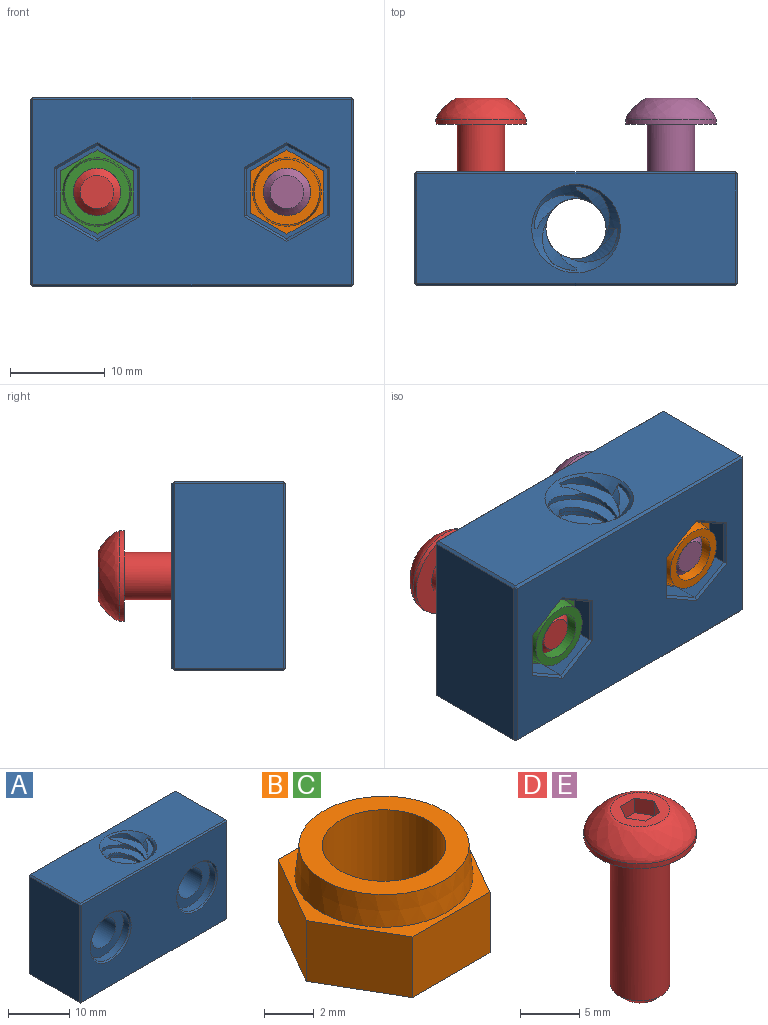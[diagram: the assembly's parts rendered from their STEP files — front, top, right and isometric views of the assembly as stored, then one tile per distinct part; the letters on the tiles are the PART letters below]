
ASSEMBLY  parts=5 mates=2
PART A: 88 faces, bbox 34x12x21.5 mm
  f0: bspline ~20.25x8.84mm, area 73.1mm2, adj f1,f18,f20,f85,f86
  f1: cylinder r=4.42mm len=19.5mm, axis (0,0,-1), area 67.9mm2, adj f0,f2,f12,f20,f84,f86
  f2: bspline ~20.25x8.84mm, area 73.1mm2, adj f1,f12,f19,f84,f86
  f3: bspline ~20.25x8.84mm, area 73.1mm2, adj f4,f17,f21,f84,f86,f87
  f4: cylinder r=4.42mm len=19.5mm, axis (0,0,-1), area 67.9mm2, adj f3,f5,f13,f21,f84,f86
  f5: bspline ~20.25x8.84mm, area 73.1mm2, adj f4,f13,f18,f84,f85,f86
  f6: bspline ~20.25x8.84mm, area 73.1mm2, adj f7,f16,f22,f84,f86
  f7: cylinder r=4.42mm len=19.5mm, axis (0,0,-1), area 67.9mm2, adj f6,f8,f14,f22,f84,f86
  f8: bspline ~20.25x8.84mm, area 73.1mm2, adj f7,f14,f17,f84,f87
  f9: bspline ~20.25x8.84mm, area 73.1mm2, adj f10,f19,f23,f84,f86
  f10: cylinder r=4.42mm len=19.5mm, axis (0,0,-1), area 67.9mm2, adj f9,f11,f15,f23,f84,f86
  f11: bspline ~20.25x8.84mm, area 73.1mm2, adj f10,f15,f16,f84,f86
  f12: plane 0.31x0.31mm, normal (0,-1,0), area 0mm2, adj f1,f2,f86
  f13: plane 0.31x0.31mm, normal (1,0,0), area 0mm2, adj f4,f5,f86
  f14: plane 0.31x0.31mm, normal (0,1,0), area 0mm2, adj f7,f8,f86
  f15: plane 0.31x0.31mm, normal (-1,0,0), area 0mm2, adj f10,f11,f86
  f16: cylinder r=3.17mm len=17mm, axis (0,0,-1), area 21.1mm2, adj f6,f11,f84,f86
  f17: cylinder r=3.17mm len=17mm, axis (0,0,-1), area 21.1mm2, adj f3,f8,f84,f87
  f18: cylinder r=3.17mm len=17mm, axis (0,0,-1), area 21.1mm2, adj f0,f5,f85,f86
  f19: cylinder r=3.17mm len=17mm, axis (0,0,-1), area 21.1mm2, adj f2,f9,f84,f86
  f20: plane 0.31x0.31mm, normal (0,-1,0), area 0mm2, adj f0,f1,f84
  f21: plane 0.31x0.31mm, normal (1,0,0), area 0mm2, adj f3,f4,f84
  f22: plane 0.31x0.31mm, normal (0,1,0), area 0mm2, adj f6,f7,f84
  f23: plane 0.31x0.31mm, normal (-1,0,0), area 0mm2, adj f9,f10,f84
  f24: plane 33.5x11.5mm, normal (0,0,1), area 316.8mm2, adj f58,f63,f66,f69,f84
  f25: cylinder r=2.75mm len=5.5mm, axis (0,-1,0), area 93.3mm2, adj f34,f36
  f26: cylinder r=2.75mm len=5.5mm, axis (0,-1,0), area 93.3mm2, adj f32,f43
  f27: plane 33.5x19.5mm, normal (0,1,0), area 513mm2, adj f53,f54,f63,f64,f72,f73,f74,f75
  f28: plane 33.5x19.5mm, normal (0,-1,0), area 511.5mm2, adj f56,f57,f65,f66,f70,f71
  f29: plane 19.5x11.5mm, normal (1,0,0), area 224.2mm2, adj f55,f64,f65,f69
  f30: plane 19.5x11.5mm, normal (-1,0,0), area 224.2mm2, adj f50,f53,f57,f58
  f31: plane 33.5x11.5mm, normal (0,0,-1), area 316.8mm2, adj f50,f54,f55,f56,f86
  f32: plane 9x9mm, normal (0,-1,0), area 39.9mm2, adj f26,f33
  f33: cylinder r=4.5mm len=9mm, axis (0,-1,0), area 38.2mm2, adj f32,f70
  f34: plane 9x9mm, normal (0,-1,0), area 39.9mm2, adj f25,f35
  f35: cylinder r=4.5mm len=9mm, axis (0,-1,0), area 38.2mm2, adj f34,f71
  f36: plane 9.82x8.5mm, normal (0,1,0), area 38.8mm2, adj f25,f37,f38,f39,f40,f41,f42
  f37: plane 4.91x4.75mm, normal (-1,0,0), area 23.3mm2, adj f36,f38,f42,f83
  f38: plane 4.75x4.25mm, normal (-0.5,0,0.87), area 23.3mm2, adj f36,f37,f39,f81
  f39: plane 4.75x4.25mm, normal (0.5,0,0.87), area 23.3mm2, adj f36,f38,f40,f79
  f40: plane 4.91x4.75mm, normal (1,0,0), area 23.3mm2, adj f36,f39,f41,f78
  f41: plane 4.75x4.25mm, normal (0.5,0,-0.87), area 23.3mm2, adj f36,f40,f42,f80
  f42: plane 4.75x4.25mm, normal (-0.5,0,-0.87), area 23.3mm2, adj f36,f37,f41,f82
  f43: plane 9.82x8.5mm, normal (0,1,0), area 38.8mm2, adj f26,f44,f45,f46,f47,f48,f49
  f44: plane 4.75x4.25mm, normal (0.5,0,-0.87), area 23.3mm2, adj f43,f45,f49,f75
  f45: plane 4.75x4.25mm, normal (-0.5,0,-0.87), area 23.3mm2, adj f43,f44,f46,f77
  f46: plane 4.91x4.75mm, normal (-1,0,0), area 23.3mm2, adj f43,f45,f47,f76
  f47: plane 4.75x4.25mm, normal (-0.5,0,0.87), area 23.3mm2, adj f43,f46,f48,f74
  f48: plane 4.75x4.25mm, normal (0.5,0,0.87), area 23.3mm2, adj f43,f47,f49,f72
  f49: plane 4.91x4.75mm, normal (1,0,0), area 23.3mm2, adj f43,f44,f48,f73
  f50: plane 11.5x0.25mm, normal (-0.71,0,-0.71), area 4.1mm2, adj f30,f31,f51,f52
  f51: plane 0.25x0.25mm, normal (-0.58,0.58,-0.58), area 0.1mm2, adj f50,f53,f54
  f52: plane 0.25x0.25mm, normal (-0.58,-0.58,-0.58), area 0.1mm2, adj f50,f56,f57
  f53: plane 19.5x0.25mm, normal (-0.71,0.71,0), area 6.9mm2, adj f27,f30,f51,f59
  f54: plane 33.5x0.25mm, normal (0,0.71,-0.71), area 11.8mm2, adj f27,f31,f51,f60
  f55: plane 11.5x0.25mm, normal (0.71,0,-0.71), area 4.1mm2, adj f29,f31,f60,f61
  f56: plane 33.5x0.25mm, normal (0,-0.71,-0.71), area 11.8mm2, adj f28,f31,f52,f61
  f57: plane 19.5x0.25mm, normal (-0.71,-0.71,0), area 6.9mm2, adj f28,f30,f52,f62
  f58: plane 11.5x0.25mm, normal (-0.71,0,0.71), area 4.1mm2, adj f24,f30,f59,f62
  f59: plane 0.25x0.25mm, normal (-0.58,0.58,0.58), area 0.1mm2, adj f53,f58,f63
  f60: plane 0.25x0.25mm, normal (0.58,0.58,-0.58), area 0.1mm2, adj f54,f55,f64
  f61: plane 0.25x0.25mm, normal (0.58,-0.58,-0.58), area 0.1mm2, adj f55,f56,f65
  f62: plane 0.25x0.25mm, normal (-0.58,-0.58,0.58), area 0.1mm2, adj f57,f58,f66
  f63: plane 33.5x0.25mm, normal (0,0.71,0.71), area 11.8mm2, adj f24,f27,f59,f67
  f64: plane 19.5x0.25mm, normal (0.71,0.71,0), area 6.9mm2, adj f27,f29,f60,f67
  f65: plane 19.5x0.25mm, normal (0.71,-0.71,0), area 6.9mm2, adj f28,f29,f61,f68
  f66: plane 33.5x0.25mm, normal (0,-0.71,0.71), area 11.8mm2, adj f24,f28,f62,f68
  f67: plane 0.25x0.25mm, normal (0.58,0.58,0.58), area 0.1mm2, adj f63,f64,f69
  f68: plane 0.25x0.25mm, normal (0.58,-0.58,0.58), area 0.1mm2, adj f65,f66,f69
  f69: plane 11.5x0.25mm, normal (0.71,0,0.71), area 4.1mm2, adj f24,f29,f67,f68
  f70: cone r=4.5mm half-angle=45deg, axis (0,-1,0), area 10.3mm2, adj f28,f33
  f71: cone r=4.5mm half-angle=45deg, axis (0,-1,0), area 10.3mm2, adj f28,f35
  f72: plane 4.5x2.74mm, normal (0.35,0.71,0.61), area 1.8mm2, adj f27,f48,f73,f74
  f73: plane 5.2x0.25mm, normal (0.71,0.71,0), area 1.8mm2, adj f27,f49,f72,f75
  f74: plane 4.5x2.74mm, normal (-0.35,0.71,0.61), area 1.8mm2, adj f27,f47,f72,f76
  f75: plane 4.5x2.74mm, normal (0.35,0.71,-0.61), area 1.8mm2, adj f27,f44,f73,f77
  f76: plane 5.2x0.25mm, normal (-0.71,0.71,0), area 1.8mm2, adj f27,f46,f74,f77
  f77: plane 4.5x2.74mm, normal (-0.35,0.71,-0.61), area 1.8mm2, adj f27,f45,f75,f76
  f78: plane 5.2x0.25mm, normal (0.71,0.71,0), area 1.8mm2, adj f27,f40,f79,f80
  f79: plane 4.5x2.74mm, normal (0.35,0.71,0.61), area 1.8mm2, adj f27,f39,f78,f81
  f80: plane 4.5x2.74mm, normal (0.35,0.71,-0.61), area 1.8mm2, adj f27,f41,f78,f82
  f81: plane 4.5x2.74mm, normal (-0.35,0.71,0.61), area 1.8mm2, adj f27,f38,f79,f83
  f82: plane 4.5x2.74mm, normal (-0.35,0.71,-0.61), area 1.8mm2, adj f27,f42,f80,f83
  f83: plane 5.2x0.25mm, normal (-0.71,0.71,0), area 1.8mm2, adj f27,f37,f81,f82
  f84: cone r=3.17mm half-angle=45deg, axis (0,0,1), area 25.6mm2, adj f1,f2,f3,f4,f5,f6,f7,f8
  f85: cone r=3.17mm half-angle=45deg, axis (0,0,1), area 1.3mm2, adj f0,f5,f18,f84
  f86: cone r=3.17mm half-angle=45deg, axis (0,0,-1), area 25.6mm2, adj f0,f1,f2,f3,f4,f5,f6,f7
  f87: cone r=3.17mm half-angle=45deg, axis (0,0,-1), area 1.3mm2, adj f3,f8,f17,f86
PART B: 11 faces, bbox 8.9x7.7x4.5 mm
  f0: plane 3.84x3mm, normal (-0.87,0.5,0), area 13.3mm2, adj f1,f5,f6,f7
  f1: plane 3.84x3mm, normal (-0.87,-0.5,0), area 13.3mm2, adj f0,f2,f6,f7
  f2: plane 4.43x3mm, normal (0,-1,0), area 13.3mm2, adj f1,f3,f6,f7
  f3: plane 3.84x3mm, normal (0.87,-0.5,0), area 13.3mm2, adj f2,f4,f6,f7
  f4: plane 3.84x3mm, normal (0.87,0.5,0), area 13.3mm2, adj f3,f5,f6,f7
  f5: plane 4.43x3mm, normal (0,1,0), area 13.3mm2, adj f0,f4,f6,f7
  f6: plane 8.87x7.68mm, normal (0,0,1), area 10.4mm2, adj f0,f1,f2,f3,f4,f5,f8
  f7: plane 8.87x7.68mm, normal (0,0,-1), area 31.4mm2, adj f0,f1,f2,f3,f4,f5,f10
  f8: cone r=3.6mm half-angle=6deg, axis (0,0,-1), area 33.4mm2, adj f6,f9
  f9: plane 6.88x6.88mm, normal (0,0,1), area 17.6mm2, adj f8,f10
  f10: cylinder r=2.5mm len=5mm, axis (0,0,1), area 70.7mm2, adj f7,f9
PART C: same geometry as B
PART D: 14 faces, bbox 9.5x9.5x18.8 mm
  f0: plane 5.01x5.01mm, normal (0,0,1), area 11.8mm2, adj f3,f4,f5,f6,f7,f8,f10
  f1: cylinder r=4.75mm len=9.5mm, axis (0,0,-1), area 14.9mm2, adj f2,f10
  f2: plane 9.5x9.5mm, normal (0,0,-1), area 51.2mm2, adj f1,f11
  f3: plane 1.5x1.5mm, normal (-0.87,-0.5,0), area 2.6mm2, adj f0,f4,f8,f9
  f4: plane 1.73x1.5mm, normal (0,-1,0), area 2.6mm2, adj f0,f3,f5,f9
  f5: plane 1.5x1.5mm, normal (0.87,-0.5,0), area 2.6mm2, adj f0,f4,f6,f9
  f6: plane 1.5x1.5mm, normal (0.87,0.5,0), area 2.6mm2, adj f0,f5,f7,f9
  f7: plane 1.73x1.5mm, normal (0,1,0), area 2.6mm2, adj f0,f6,f8,f9
  f8: plane 1.5x1.5mm, normal (-0.87,0.5,0), area 2.6mm2, adj f0,f3,f7,f9
  f9: plane 3.46x3mm, normal (0,0,1), area 7.8mm2, adj f3,f4,f5,f6,f7,f8
  f10: bspline ~9.5x9.5mm, area 78.3mm2, adj f0,f1
  f11: cylinder r=2.5mm len=15.25mm, axis (0,0,1), area 239.5mm2, adj f2,f13
  f12: plane 3.5x3.5mm, normal (0,0,-1), area 9.6mm2, adj f13
  f13: cone r=1.75mm half-angle=45deg, axis (0,0,1), area 14.2mm2, adj f11,f12
PART E: same geometry as D
PLACE A rot(axis=(1,0,0),180deg) t=(-35.32,-6,-54.47)mm
PLACE B rot(axis=(0.58,-0.58,0.58),120deg) t=(-25.32,-7,-64.47)mm
PLACE C rot(axis=(0.58,-0.58,0.58),120deg) t=(-45.32,-7,-64.47)mm
PLACE D rot(axis=(-1,0,0),90deg) t=(-20.32,5,-64.47)mm
PLACE E rot(axis=(-1,0,0),90deg) t=(-0.32,5,-64.47)mm
MATE fastened C.f8 <-> A.f25  axis (0,1,0) through (-45.32,-7,-64.47)mm
MATE fastened A.f25 <-> D.f1  axis (0,1,0) through (-45.32,0,-64.47)mm
